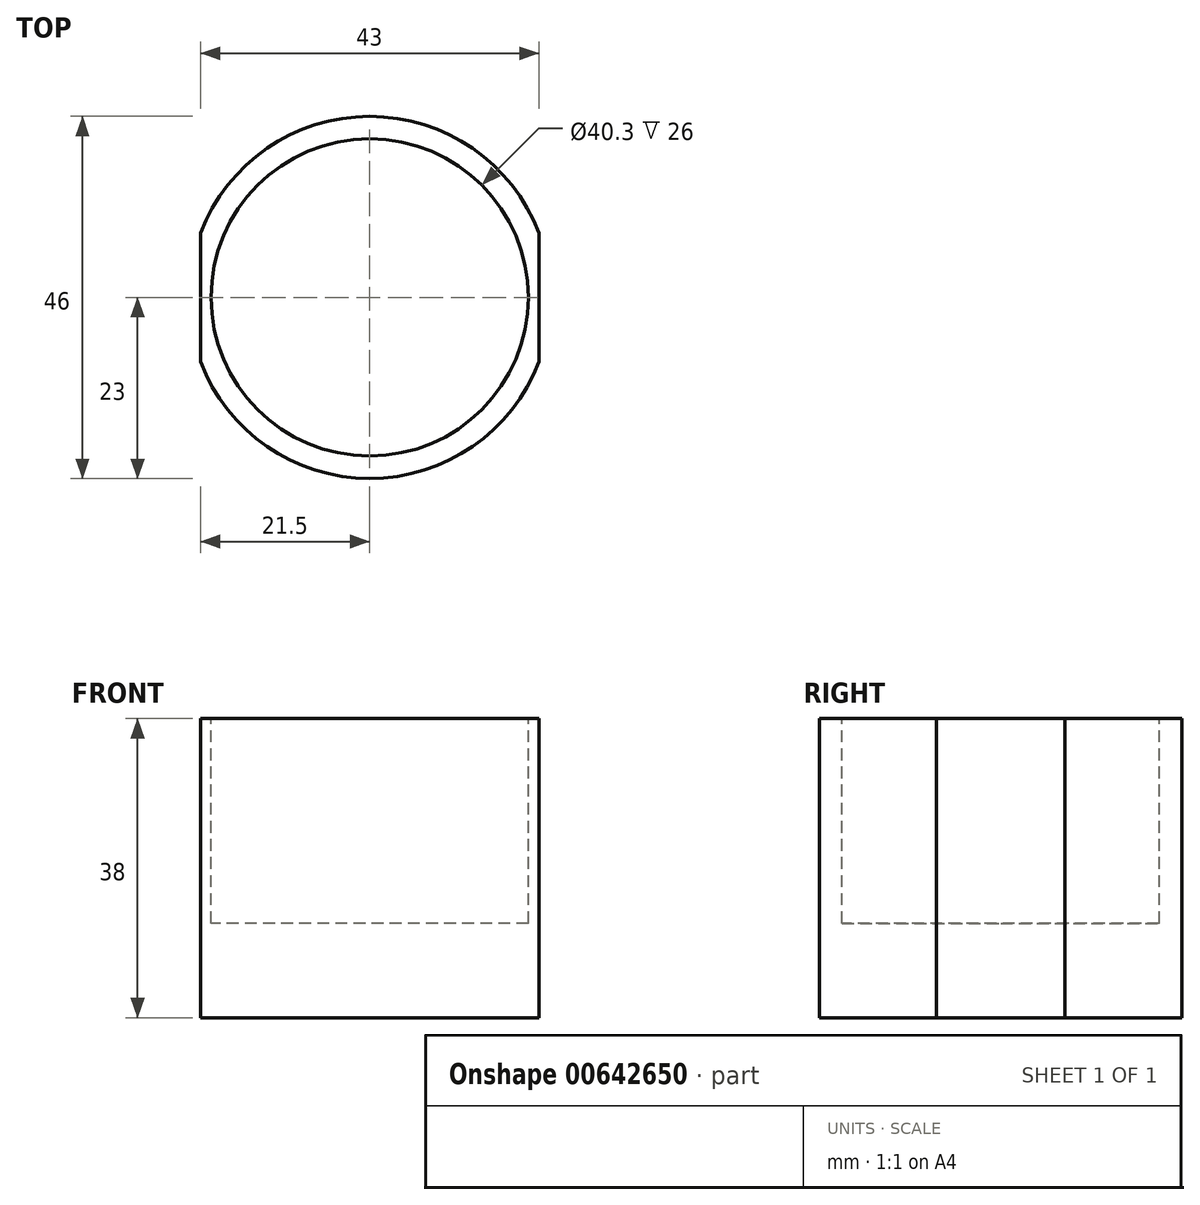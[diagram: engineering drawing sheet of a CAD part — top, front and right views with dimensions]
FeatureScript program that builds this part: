
annotation { "Feature Type Name" : "Feature", "Feature Type Description" : "" }
export const myFeature = defineFeature(function(context is Context, id is Id, definition is map)
    precondition{}
    {
        {
            var Q0;
            Q0=qCreatedBy(makeId("Top.planeOp"),FACE);
            var sketch = newSketch(context, id + "F0", { "sketchPlane" : qUnion([Q0])});
            skArc(sketch, "E0", {"start": v(21.5, 8.17) * mm, "mid": v(0, 23) * mm, "end": v(-21.5, 8.17) * mm});
            skLineSegment(sketch, "E1", {"start": v(21.5, 8.17) * mm, "end": v(21.5, -8.17) * mm});
            skLineSegment(sketch, "E2.MirrorCS", {"start": v(-21.5, 8.17) * mm, "end": v(-21.5, -8.17) * mm});
            skArc(sketch, "E3.trimOffspring", {"start": v(-21.5, -8.17) * mm, "mid": v(0, -23) * mm, "end": v(21.5, -8.17) * mm});
            skSolve(sketch);
        }
        {
            var Q0;
            Q0=makeQuery(id+"F0.imprint","IMPRINT",FACE,{"disambiguationData":[TD([[makeQuery(id+"F0.imprint","IMPRINT",EDGE,{"derivedFrom":sQuery(id+"F0.wireOp",EDGE,"E0")}),1.0]])]});
            extrude(context, id + "F1", {"entities" : qUnion([Q0]), "depth" : 38 * mm, "offsetDistance" : 25 * mm});
        }
        {
            var Q0;
            Q0=makeQuery(id+"F1.opExtrude","CAP_FACE",FACE,{"disambiguationData":[OSD([sQuery(id+"F0.wireOp",EDGE,"E0"),sQuery(id+"F0.wireOp",EDGE,"E1"),sQuery(id+"F0.wireOp",EDGE,"E2.MirrorCS"),sQuery(id+"F0.wireOp",EDGE,"E3.trimOffspring")])],"isStart":false});
            var sketch = newSketch(context, id + "F2", { "sketchPlane" : qUnion([Q0])});
            skCircle(sketch, "E4", {"center": v(0, 0) * mm, "radius": 20.15 * mm});
            skSolve(sketch);
        }
        {
            var Q0;
            Q0=makeQuery(id+"F2.imprint","IMPRINT",FACE,{"disambiguationData":[TD([[makeQuery(id+"F2.imprint","IMPRINT",EDGE,{"derivedFrom":sQuery(id+"F2.wireOp",EDGE,"E4")}),1.0]])]});
            extrude(context, id + "F3", {"entities" : qUnion([Q0]), "operationType" : NewBodyOperationType.REMOVE, "oppositeDirection" : true, "depth" : 26 * mm, "offsetDistance" : 25 * mm});
        }
    });
